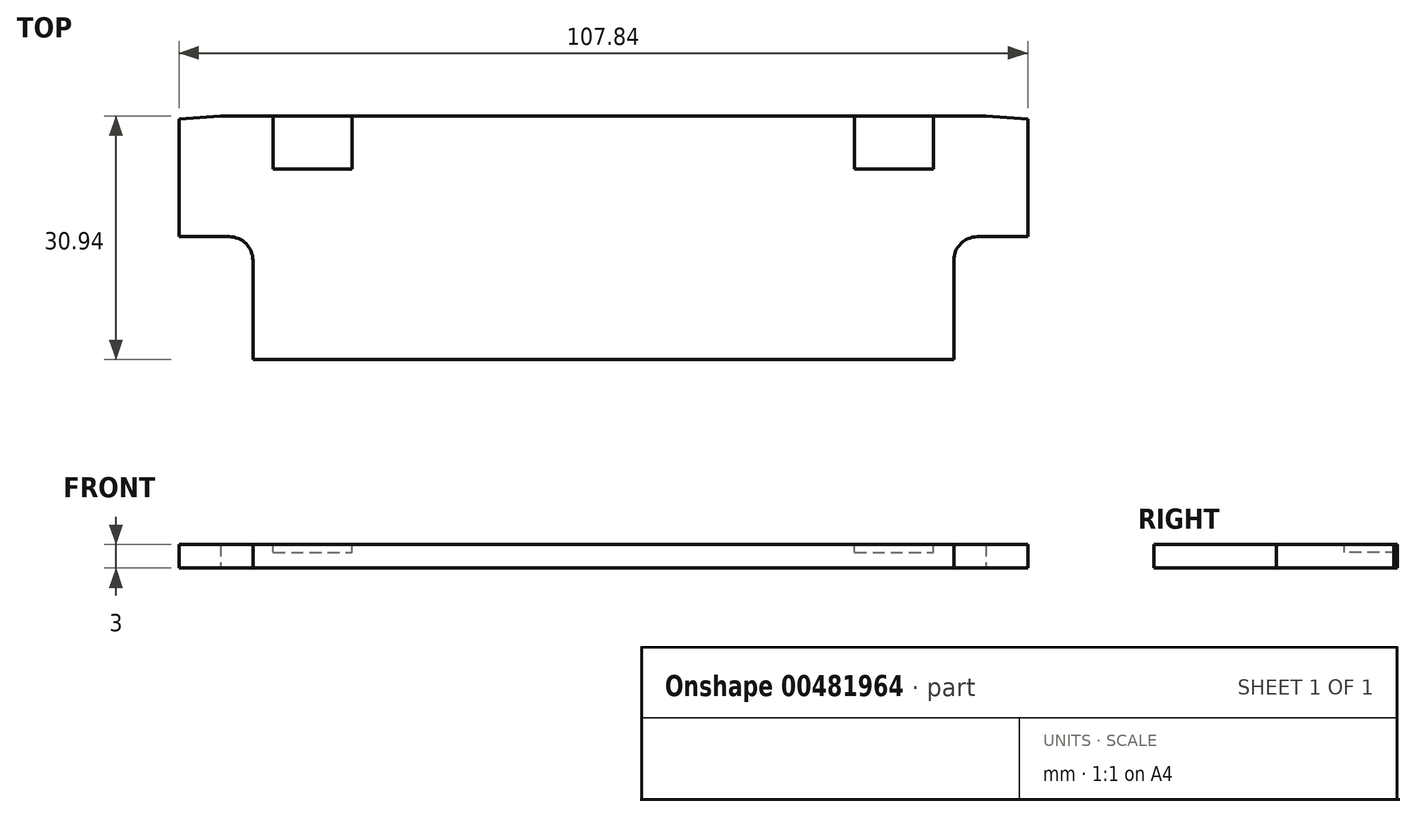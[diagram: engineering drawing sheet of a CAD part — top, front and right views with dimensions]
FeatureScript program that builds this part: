
annotation { "Feature Type Name" : "Feature", "Feature Type Description" : "" }
export const myFeature = defineFeature(function(context is Context, id is Id, definition is map)
    precondition{}
    {
        {
            var Q0;
            Q0=qCreatedBy(makeId("Top.planeOp"),FACE);
            var sketch = newSketch(context, id + "F0", { "sketchPlane" : qUnion([Q0])});
            skLineSegment(sketch, "E0.bottom", {"start": v(-48.6, 15.47) * mm, "end": v(48.59, 15.47) * mm});
            skLineSegment(sketch, "E0.top", {"start": v(-44.52, -15.48) * mm, "end": v(44.52, -15.48) * mm});
            skLineSegment(sketch, "E0.left", {"start": v(-53.92, 15.05) * mm, "end": v(-53.92, 0.11) * mm});
            skLineSegment(sketch, "E0.right", {"start": v(53.92, 15.05) * mm, "end": v(53.92, 0.11) * mm});
            skPoint(sketch, "E0.middle", {"position": v(0, 0) * mm});
            skLineSegment(sketch, "E1", {"start": v(53.92, 0.11) * mm, "end": v(47.52, 0.11) * mm});
            skLineSegment(sketch, "E2", {"start": v(44.52, -2.89) * mm, "end": v(44.52, -15.48) * mm});
            skLineSegment(sketch, "E3", {"start": v(-53.92, 0.11) * mm, "end": v(-47.52, 0.11) * mm});
            skLineSegment(sketch, "E4", {"start": v(-44.52, -2.89) * mm, "end": v(-44.52, -15.48) * mm});
            skPoint(sketch, "E5.orphan", {"position": v(53.92, -15.48) * mm});
            skPoint(sketch, "E6.orphan", {"position": v(-53.92, -15.48) * mm});
            skPoint(sketch, "E7.visualSharp", {"position": v(-44.52, 0.11) * mm});
            skArc(sketch, "E7.filletArc", {"start": v(-44.52, -2.89) * mm, "mid": v(-45.4, -0.76) * mm, "end": v(-47.52, 0.11) * mm});
            skPoint(sketch, "E8.visualSharp", {"position": v(44.52, 0.11) * mm});
            skArc(sketch, "E8.filletArc", {"start": v(47.52, 0.11) * mm, "mid": v(45.4, -0.76) * mm, "end": v(44.52, -2.89) * mm});
            skLineSegment(sketch, "E9", {"start": v(-53.92, 15.05) * mm, "end": v(-48.6, 15.47) * mm});
            skLineSegment(sketch, "E10", {"start": v(53.92, 15.05) * mm, "end": v(48.59, 15.47) * mm});
            skPoint(sketch, "E11.orphan", {"position": v(-53.92, 15.47) * mm});
            skPoint(sketch, "E12.orphan", {"position": v(53.92, 15.47) * mm});
            skSolve(sketch);
        }
        {
            var Q0;
            Q0 = qSketchRegion(id + "F0", true);
            extrude(context, id + "F1", {"entities" : qUnion([Q0]), "depth" : 3 * mm});
        }
        {
            var Q0;
            Q0=makeQuery(id+"F1.opExtrude","CAP_FACE",FACE,{"disambiguationData":[OSD([sQuery(id+"F0.wireOp",EDGE,"E0.bottom"),sQuery(id+"F0.wireOp",EDGE,"E0.top"),sQuery(id+"F0.wireOp",EDGE,"E0.left"),sQuery(id+"F0.wireOp",EDGE,"E0.right"),sQuery(id+"F0.wireOp",EDGE,"E1"),sQuery(id+"F0.wireOp",EDGE,"E2"),sQuery(id+"F0.wireOp",EDGE,"E3"),sQuery(id+"F0.wireOp",EDGE,"E4"),sQuery(id+"F0.wireOp",EDGE,"E7.filletArc"),sQuery(id+"F0.wireOp",EDGE,"E8.filletArc"),sQuery(id+"F0.wireOp",EDGE,"E9"),sQuery(id+"F0.wireOp",EDGE,"E10")])],"isStart":false});
            var sketch = newSketch(context, id + "F2", { "sketchPlane" : qUnion([Q0])});
            skLineSegment(sketch, "E13.bottom", {"start": v(-41.92, 15.47) * mm, "end": v(-31.92, 15.47) * mm});
            skLineSegment(sketch, "E13.top", {"start": v(-41.92, 8.72) * mm, "end": v(-31.92, 8.72) * mm});
            skLineSegment(sketch, "E13.left", {"start": v(-41.92, 15.47) * mm, "end": v(-41.92, 8.72) * mm});
            skLineSegment(sketch, "E13.right", {"start": v(-31.92, 15.47) * mm, "end": v(-31.92, 8.72) * mm});
            skLineSegment(sketch, "E14.bottom", {"start": v(31.92, 15.47) * mm, "end": v(41.92, 15.47) * mm});
            skLineSegment(sketch, "E14.top", {"start": v(31.92, 8.72) * mm, "end": v(41.92, 8.72) * mm});
            skLineSegment(sketch, "E14.left", {"start": v(31.92, 15.47) * mm, "end": v(31.92, 8.72) * mm});
            skLineSegment(sketch, "E14.right", {"start": v(41.92, 15.47) * mm, "end": v(41.92, 8.72) * mm});
            skSolve(sketch);
        }
        {
            var Q0;
            Q0 = qSketchRegion(id + "F2", true);
            extrude(context, id + "F3", {"entities" : qUnion([Q0]), "operationType" : NewBodyOperationType.REMOVE, "oppositeDirection" : true, "depth" : 1 * mm});
        }
    });
